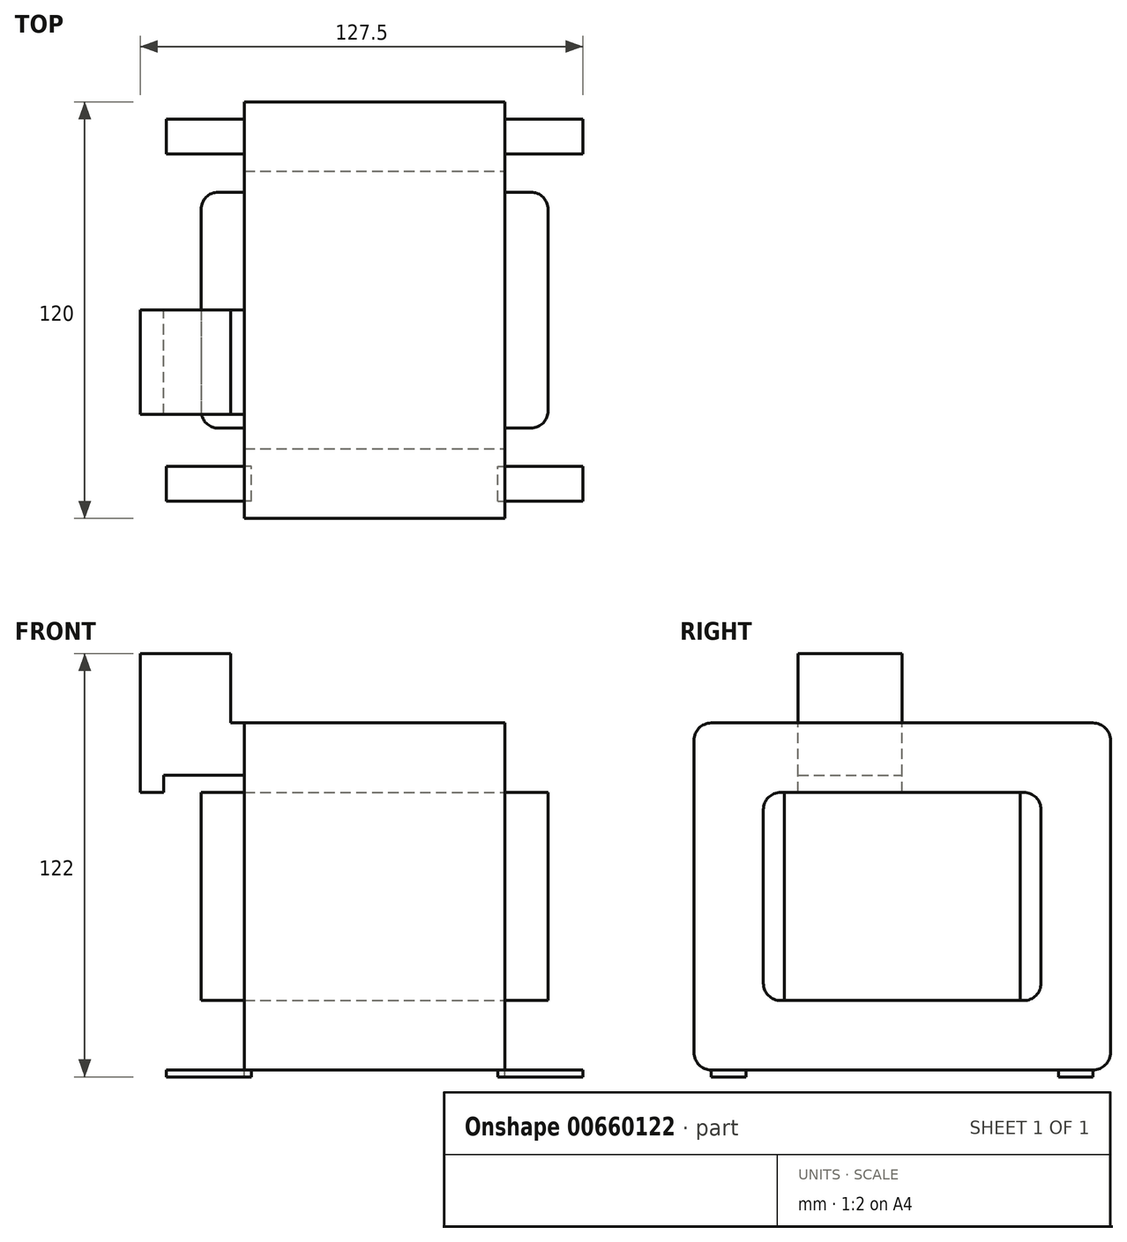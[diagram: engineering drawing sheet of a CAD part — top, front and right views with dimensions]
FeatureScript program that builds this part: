
annotation { "Feature Type Name" : "Feature", "Feature Type Description" : "" }
export const myFeature = defineFeature(function(context is Context, id is Id, definition is map)
    precondition{}
    {
        {
            var Q0;
            Q0=qCreatedBy(makeId("Top.planeOp"),FACE);
            var sketch = newSketch(context, id + "F0", { "sketchPlane" : qUnion([Q0])});
            skLineSegment(sketch, "E0.bottom", {"start": v(-37.5, 60) * mm, "end": v(37.5, 60) * mm});
            skLineSegment(sketch, "E0.top", {"start": v(-37.5, -60) * mm, "end": v(37.5, -60) * mm});
            skLineSegment(sketch, "E0.left", {"start": v(-37.5, 60) * mm, "end": v(-37.5, -60) * mm});
            skLineSegment(sketch, "E0.right", {"start": v(37.5, 60) * mm, "end": v(37.5, -60) * mm});
            skPoint(sketch, "E0.middle", {"position": v(0, 0) * mm});
            skSolve(sketch);
        }
        {
            var Q0;
            Q0=makeQuery(id+"F0.imprint","IMPRINT",FACE,{"disambiguationData":[TD([[makeQuery(id+"F0.imprint","IMPRINT",EDGE,{"derivedFrom":sQuery(id+"F0.wireOp",EDGE,"E0.bottom")}),-1.0]])]});
            extrude(context, id + "F1", {"entities" : qUnion([Q0]), "depth" : 100 * mm});
        }
        {
            var Q0;
            Q0=makeQuery(id+"F1.opExtrude","SWEPT_FACE",FACE,{"disambiguationData":[OSD([sQuery(id+"F0.wireOp",EDGE,"E0.right")])]});
            var sketch = newSketch(context, id + "F2", { "sketchPlane" : qUnion([Q0])});
            skLineSegment(sketch, "E1.bottom", {"start": v(-40, 80) * mm, "end": v(40, 80) * mm});
            skLineSegment(sketch, "E1.top", {"start": v(-40, 20) * mm, "end": v(40, 20) * mm});
            skLineSegment(sketch, "E1.left", {"start": v(-40, 80) * mm, "end": v(-40, 20) * mm});
            skLineSegment(sketch, "E1.right", {"start": v(40, 80) * mm, "end": v(40, 20) * mm});
            skPoint(sketch, "E1.middle", {"position": v(0, 50) * mm});
            skPoint(sketch, "E1.middle.positionSnap0", {"position": v(0, 100) * mm});
            skPoint(sketch, "E1.centerSnap0", {"position": v(0, 100) * mm});
            skSolve(sketch);
        }
        {
            var Q0;
            Q0=makeQuery(id+"F2.imprint","IMPRINT",FACE,{"disambiguationData":[TD([[makeQuery(id+"F2.imprint","IMPRINT",EDGE,{"derivedFrom":sQuery(id+"F2.wireOp",EDGE,"E1.bottom")}),-1.0]])]});
            extrude(context, id + "F3", {"entities" : qUnion([Q0]), "operationType" : NewBodyOperationType.REMOVE, "endBound" : BoundingType.THROUGH_ALL, "oppositeDirection" : true, "depth" : 25 * mm});
        }
        {
            var Q0;
            Q0=makeQuery(id+"F3.boolean.opBoolean","COPY",EDGE,{"derivedFrom":makeQuery(id+"F3.opExtrude","SWEPT_EDGE",EDGE,{"disambiguationData":[OSD([sQuery(id+"F2.wireOp",EDGE,"E1.top"),sQuery(id+"F2.wireOp",EDGE,"E1.right")])]})});
            var Q1;
            Q1=makeQuery(id+"F1.opExtrude","CAP_EDGE",EDGE,{"disambiguationData":[OSD([sQuery(id+"F0.wireOp",EDGE,"E0.top")])],"isStart":false});
            var Q2;
            Q2=makeQuery(id+"F1.opExtrude","CAP_EDGE",EDGE,{"disambiguationData":[OSD([sQuery(id+"F0.wireOp",EDGE,"E0.top")])],"isStart":true});
            var Q3;
            Q3=makeQuery(id+"F3.boolean.opBoolean","COPY",EDGE,{"derivedFrom":makeQuery(id+"F3.opExtrude","SWEPT_EDGE",EDGE,{"disambiguationData":[OSD([sQuery(id+"F2.wireOp",EDGE,"E1.top"),sQuery(id+"F2.wireOp",EDGE,"E1.left")])]})});
            var Q4;
            Q4=makeQuery(id+"F1.opExtrude","CAP_EDGE",EDGE,{"disambiguationData":[OSD([sQuery(id+"F0.wireOp",EDGE,"E0.bottom")])],"isStart":true});
            var Q5;
            Q5=makeQuery(id+"F1.opExtrude","CAP_EDGE",EDGE,{"disambiguationData":[OSD([sQuery(id+"F0.wireOp",EDGE,"E0.bottom")])],"isStart":false});
            var Q6;
            Q6=makeQuery(id+"F3.boolean.opBoolean","COPY",EDGE,{"derivedFrom":makeQuery(id+"F3.opExtrude","SWEPT_EDGE",EDGE,{"disambiguationData":[OSD([sQuery(id+"F2.wireOp",EDGE,"E1.bottom"),sQuery(id+"F2.wireOp",EDGE,"E1.left")])]})});
            var Q7;
            Q7=makeQuery(id+"F3.boolean.opBoolean","COPY",EDGE,{"derivedFrom":makeQuery(id+"F3.opExtrude","SWEPT_EDGE",EDGE,{"disambiguationData":[OSD([sQuery(id+"F2.wireOp",EDGE,"E1.bottom"),sQuery(id+"F2.wireOp",EDGE,"E1.right")])]})});
            fillet(context, id + "F4", {"entities" : qUnion([Q0, Q1, Q2, Q3, Q4, Q5, Q6, Q7]), "radius" : 5 * mm, "allowEdgeOverflow" : false});
        }
        {
            var Q0;
            Q0=makeQuery(id+"F3.boolean.opBoolean","COPY",FACE,{"derivedFrom":makeQuery(id+"F3.opExtrude","SWEPT_FACE",FACE,{"disambiguationData":[OSD([sQuery(id+"F2.wireOp",EDGE,"E1.top")])]})});
            var sketch = newSketch(context, id + "F5", { "sketchPlane" : qUnion([Q0])});
            skLineSegment(sketch, "E2.bottom", {"start": v(-45, 34) * mm, "end": v(45, 34) * mm});
            skLineSegment(sketch, "E2.top", {"start": v(-45, -34) * mm, "end": v(45, -34) * mm});
            skLineSegment(sketch, "E2.left", {"start": v(-50, 29) * mm, "end": v(-50, -29) * mm});
            skLineSegment(sketch, "E2.right", {"start": v(50, 29) * mm, "end": v(50, -29) * mm});
            skPoint(sketch, "E2.middle", {"position": v(0, 0) * mm});
            skPoint(sketch, "E3.visualSharp", {"position": v(-50, 34) * mm});
            skArc(sketch, "E3.filletArc", {"start": v(-45, 34) * mm, "mid": v(-48.54, 32.54) * mm, "end": v(-50, 29) * mm});
            skPoint(sketch, "E4.visualSharp", {"position": v(-50, -34) * mm});
            skArc(sketch, "E4.filletArc", {"start": v(-50, -29) * mm, "mid": v(-48.54, -32.54) * mm, "end": v(-45, -34) * mm});
            skPoint(sketch, "E5.visualSharp", {"position": v(50, -34) * mm});
            skArc(sketch, "E5.filletArc", {"start": v(45, -34) * mm, "mid": v(48.54, -32.54) * mm, "end": v(50, -29) * mm});
            skPoint(sketch, "E6.visualSharp", {"position": v(50, 34) * mm});
            skArc(sketch, "E6.filletArc", {"start": v(50, 29) * mm, "mid": v(48.54, 32.54) * mm, "end": v(45, 34) * mm});
            skSolve(sketch);
        }
        {
            var Q0;
            Q0=makeQuery(id+"F5.imprint","IMPRINT",FACE,{"disambiguationData":[TD([[makeQuery(id+"F5.imprint","IMPRINT",EDGE,{"derivedFrom":sQuery(id+"F5.wireOp",EDGE,"E2.left")}),1.0]])]});
            var Q1;
            {var subQ0=sQuery(id+"F5.wireOp",EDGE,"E2.bottom");var subQ1=sQuery(id+"F2.wireOp",EDGE,"E1.top");var subQ4=makeQuery(id+"F3.boolean.opBoolean","COPY",EDGE,{"derivedFrom":makeQuery(id+"F3.opExtrude","CAP_EDGE",EDGE,{"disambiguationData":[OSD([subQ1])],"isStart":true})});var subQ5=makeQuery(id+"F5.imprint","INTERSECT",VERTEX,{"derivedFrom":[subQ4,subQ0]});Q1=makeQuery(id+"F5.imprint","IMPRINT",FACE,{"disambiguationData":[TD([[makeQuery(id+"F5.imprint","IMPRINT",EDGE,{"disambiguationData":[TD([[subQ5,1.0]])],"derivedFrom":subQ4}),1.0]])]});}
            var Q2;
            Q2=makeQuery(id+"F5.imprint","IMPRINT",FACE,{"disambiguationData":[TD([[makeQuery(id+"F5.imprint","IMPRINT",EDGE,{"derivedFrom":sQuery(id+"F5.wireOp",EDGE,"E2.right")}),-1.0]])]});
            extrude(context, id + "F6", {"entities" : qUnion([Q0, Q1, Q2]), "depth" : 60 * mm});
        }
        {
            var Q0;
            Q0=makeQuery(id+"F1.opExtrude","CAP_FACE",FACE,{"disambiguationData":[OSD([sQuery(id+"F0.wireOp",EDGE,"E0.bottom"),sQuery(id+"F0.wireOp",EDGE,"E0.top"),sQuery(id+"F0.wireOp",EDGE,"E0.left"),sQuery(id+"F0.wireOp",EDGE,"E0.right")])],"isStart":true});
            var sketch = newSketch(context, id + "F7", { "sketchPlane" : qUnion([Q0])});
            skLineSegment(sketch, "E7.0.0", {"start": v(-37.5, 55) * mm, "end": v(-37.5, 60) * mm});
            skLineSegment(sketch, "E7.0.1", {"start": v(37.5, 55) * mm, "end": v(-37.5, 55) * mm});
            skLineSegment(sketch, "E7.0.2", {"start": v(37.5, 55) * mm, "end": v(37.5, 60) * mm});
            skLineSegment(sketch, "E7.0.3", {"start": v(37.5, 60) * mm, "end": v(-37.5, 60) * mm});
            skLineSegment(sketch, "E8.0.0", {"start": v(37.5, -55) * mm, "end": v(37.5, 55) * mm});
            skLineSegment(sketch, "E8.0.2", {"start": v(-37.5, 55) * mm, "end": v(-37.5, -55) * mm});
            skLineSegment(sketch, "E8.0.3", {"start": v(-37.5, -55) * mm, "end": v(37.5, -55) * mm});
            skLineSegment(sketch, "E9.0.0", {"start": v(-37.5, -60) * mm, "end": v(-37.5, -55) * mm});
            skLineSegment(sketch, "E9.0.1", {"start": v(37.5, -60) * mm, "end": v(-37.5, -60) * mm});
            skLineSegment(sketch, "E9.0.2", {"start": v(37.5, -60) * mm, "end": v(37.5, -55) * mm});
            skLineSegment(sketch, "E9.0.3", {"start": v(37.5, -55) * mm, "end": v(-37.5, -55) * mm});
            skLineSegment(sketch, "E10.bottom", {"start": v(-37.5, -55) * mm, "end": v(-60, -55) * mm});
            skLineSegment(sketch, "E10.top", {"start": v(-37.5, -45) * mm, "end": v(-60, -45) * mm});
            skLineSegment(sketch, "E10.left", {"start": v(-37.5, -55) * mm, "end": v(-37.5, -45) * mm});
            skLineSegment(sketch, "E10.right", {"start": v(-60, -55) * mm, "end": v(-60, -45) * mm});
            skLineSegment(sketch, "E11.bottom", {"start": v(37.5, -55) * mm, "end": v(60, -55) * mm});
            skLineSegment(sketch, "E11.top", {"start": v(37.5, -45) * mm, "end": v(60, -45) * mm});
            skLineSegment(sketch, "E11.left", {"start": v(37.5, -55) * mm, "end": v(37.5, -45) * mm});
            skLineSegment(sketch, "E11.right", {"start": v(60, -55) * mm, "end": v(60, -45) * mm});
            skLineSegment(sketch, "E12", {"start": v(-37.5, 0) * mm, "end": v(37.5, 0) * mm, "construction": true});
            skLineSegment(sketch, "E13.MirrorCS", {"start": v(-37.5, 45) * mm, "end": v(-60, 45) * mm});
            skLineSegment(sketch, "E14.MirrorCS", {"start": v(-60, 55) * mm, "end": v(-60, 45) * mm});
            skLineSegment(sketch, "E15.MirrorCS", {"start": v(-37.5, 55) * mm, "end": v(-60, 55) * mm});
            skLineSegment(sketch, "E16.MirrorCS", {"start": v(60, 55) * mm, "end": v(60, 45) * mm});
            skLineSegment(sketch, "E17.MirrorCS", {"start": v(37.5, 45) * mm, "end": v(60, 45) * mm});
            skLineSegment(sketch, "E18.MirrorCS", {"start": v(37.5, 55) * mm, "end": v(60, 55) * mm});
            skLineSegment(sketch, "E19.bottom", {"start": v(-37.5, -55) * mm, "end": v(-35.5, -55) * mm});
            skLineSegment(sketch, "E19.top", {"start": v(-37.5, -45) * mm, "end": v(-35.5, -45) * mm});
            skLineSegment(sketch, "E19.right", {"start": v(-35.5, -55) * mm, "end": v(-35.5, -45) * mm});
            skLineSegment(sketch, "E20", {"start": v(0, 55) * mm, "end": v(0, -55) * mm, "construction": true});
            skLineSegment(sketch, "E21.MirrorCS", {"start": v(35.5, -55) * mm, "end": v(35.5, -45) * mm});
            skLineSegment(sketch, "E22.MirrorCS", {"start": v(37.5, -45) * mm, "end": v(35.5, -45) * mm});
            skLineSegment(sketch, "E23.MirrorCS", {"start": v(35.5, 55) * mm, "end": v(35.5, 45) * mm});
            skLineSegment(sketch, "E24.MirrorCS", {"start": v(37.5, 45) * mm, "end": v(35.5, 45) * mm});
            skLineSegment(sketch, "E25.MirrorCS", {"start": v(-37.5, 45) * mm, "end": v(-35.5, 45) * mm});
            skLineSegment(sketch, "E26.MirrorCS", {"start": v(-35.5, 55) * mm, "end": v(-35.5, 45) * mm});
            skSolve(sketch);
        }
        {
            var Q0;
            {var subQ2=sQuery(id+"F7.wireOp",EDGE,"E13.MirrorCS");Q0=makeQuery(id+"F7.imprint","IMPRINT",FACE,{"disambiguationData":[TD([[makeQuery(id+"F7.imprint","IMPRINT",EDGE,{"derivedFrom":subQ2}),-1.0]])]});}
            var Q1;
            Q1=makeQuery(id+"F7.imprint","IMPRINT",FACE,{"disambiguationData":[TD([[makeQuery(id+"F7.imprint","IMPRINT",EDGE,{"derivedFrom":sQuery(id+"F7.wireOp",EDGE,"E16.MirrorCS")}),-1.0]])]});
            var Q2;
            Q2=makeQuery(id+"F7.imprint","IMPRINT",FACE,{"disambiguationData":[TD([[makeQuery(id+"F7.imprint","IMPRINT",EDGE,{"derivedFrom":sQuery(id+"F7.wireOp",EDGE,"E11.bottom")}),1.0]])]});
            var Q3;
            Q3=makeQuery(id+"F7.imprint","IMPRINT",FACE,{"disambiguationData":[TD([[makeQuery(id+"F7.imprint","IMPRINT",EDGE,{"derivedFrom":sQuery(id+"F7.wireOp",EDGE,"E10.bottom")}),-1.0]])]});
            var Q4;
            {var subQ4=sQuery(id+"F7.wireOp",EDGE,"E25.MirrorCS");Q4=makeQuery(id+"F7.imprint","IMPRINT",FACE,{"disambiguationData":[TD([[makeQuery(id+"F7.imprint","IMPRINT",EDGE,{"derivedFrom":subQ4}),1.0]])]});}
            var Q5;
            {var subQ4=sQuery(id+"F7.wireOp",EDGE,"E23.MirrorCS");Q5=makeQuery(id+"F7.imprint","IMPRINT",FACE,{"disambiguationData":[TD([[makeQuery(id+"F7.imprint","IMPRINT",EDGE,{"derivedFrom":subQ4}),1.0]])]});}
            var Q6;
            {var subQ0=sQuery(id+"F7.wireOp",EDGE,"E11.left");Q6=makeQuery(id+"F7.imprint","IMPRINT",FACE,{"disambiguationData":[TD([[makeQuery(id+"F7.imprint","IMPRINT",EDGE,{"derivedFrom":subQ0}),1.0]])]});}
            var Q7;
            Q7=makeQuery(id+"F7.imprint","IMPRINT",FACE,{"disambiguationData":[TD([[makeQuery(id+"F7.imprint","IMPRINT",EDGE,{"derivedFrom":sQuery(id+"F7.wireOp",EDGE,"E19.bottom")}),1.0]])]});
            extrude(context, id + "F8", {"entities" : qUnion([Q0, Q1, Q2, Q3, Q4, Q5, Q6, Q7]), "operationType" : NewBodyOperationType.ADD, "depth" : 2 * mm});
        }
        {
            var Q0;
            Q0=qCreatedBy(makeId("Front.planeOp"),FACE);
            var sketch = newSketch(context, id + "F9", { "sketchPlane" : qUnion([Q0])});
            skLineSegment(sketch, "E27.0.1", {"start": v(-37.5, 100) * mm, "end": v(37.5, 100) * mm});
            skLineSegment(sketch, "E27.0.3", {"start": v(37.5, 100) * mm, "end": v(-37.5, 100) * mm});
            skLineSegment(sketch, "E28.0.0", {"start": v(37.5, 95) * mm, "end": v(37.5, 5) * mm});
            skLineSegment(sketch, "E28.0.1", {"start": v(37.5, 5) * mm, "end": v(37.5, 0) * mm});
            skLineSegment(sketch, "E28.0.5", {"start": v(37.5, 0) * mm, "end": v(37.5, 5) * mm});
            skLineSegment(sketch, "E28.0.6", {"start": v(37.5, 5) * mm, "end": v(37.5, 95) * mm});
            skLineSegment(sketch, "E28.0.7", {"start": v(37.5, 95) * mm, "end": v(37.5, 100) * mm});
            skLineSegment(sketch, "E28.0.9", {"start": v(37.5, 100) * mm, "end": v(37.5, 95) * mm});
            skLineSegment(sketch, "E29", {"start": v(37.5, 100) * mm, "end": v(47.5, 115) * mm});
            skLineSegment(sketch, "E30", {"start": v(47.5, 115) * mm, "end": v(47.5, 119) * mm});
            skLineSegment(sketch, "E31", {"start": v(47.5, 119) * mm, "end": v(57.5, 119) * mm});
            skLineSegment(sketch, "E32", {"start": v(57.5, 119) * mm, "end": v(57.5, 80) * mm});
            skLineSegment(sketch, "E33", {"start": v(57.5, 80) * mm, "end": v(52.5, 80) * mm});
            skLineSegment(sketch, "E34", {"start": v(52.5, 80) * mm, "end": v(37.5, 90) * mm});
            skLineSegment(sketch, "E35", {"start": v(-37.5, 100) * mm, "end": v(-41.5, 100) * mm});
            skLineSegment(sketch, "E36", {"start": v(-41.5, 100) * mm, "end": v(-41.5, 120) * mm});
            skLineSegment(sketch, "E37", {"start": v(-41.5, 120) * mm, "end": v(-67.5, 120) * mm});
            skLineSegment(sketch, "E38", {"start": v(-67.5, 120) * mm, "end": v(-67.5, 80) * mm});
            skLineSegment(sketch, "E39", {"start": v(-67.5, 80) * mm, "end": v(-60.76, 80) * mm});
            skLineSegment(sketch, "E40", {"start": v(-60.76, 80) * mm, "end": v(-60.76, 85) * mm});
            skLineSegment(sketch, "E41", {"start": v(-60.76, 85) * mm, "end": v(-37.5, 85) * mm});
            skLineSegment(sketch, "E42", {"start": v(-37.5, 85) * mm, "end": v(-37.5, 100) * mm});
            skSolve(sketch);
        }
        {
            var Q0;
            Q0=makeQuery(id+"F9.imprint","IMPRINT",FACE,{"disambiguationData":[TD([[makeQuery(id+"F9.imprint","IMPRINT",EDGE,{"derivedFrom":sQuery(id+"F9.wireOp",EDGE,"E35")}),1.0]])]});
            var Q1;
            {var subQ0=sQuery(id+"F9.wireOp",EDGE,"E28.0.9");Q1=makeQuery(id+"F9.imprint","IMPRINT",FACE,{"disambiguationData":[TD([[makeQuery(id+"F9.imprint","IMPRINT",EDGE,{"derivedFrom":subQ0}),1.0]])]});}
            extrude(context, id + "F10", {"entities" : qUnion([Q0, Q1]), "depth" : 30 * mm});
        }
    });
